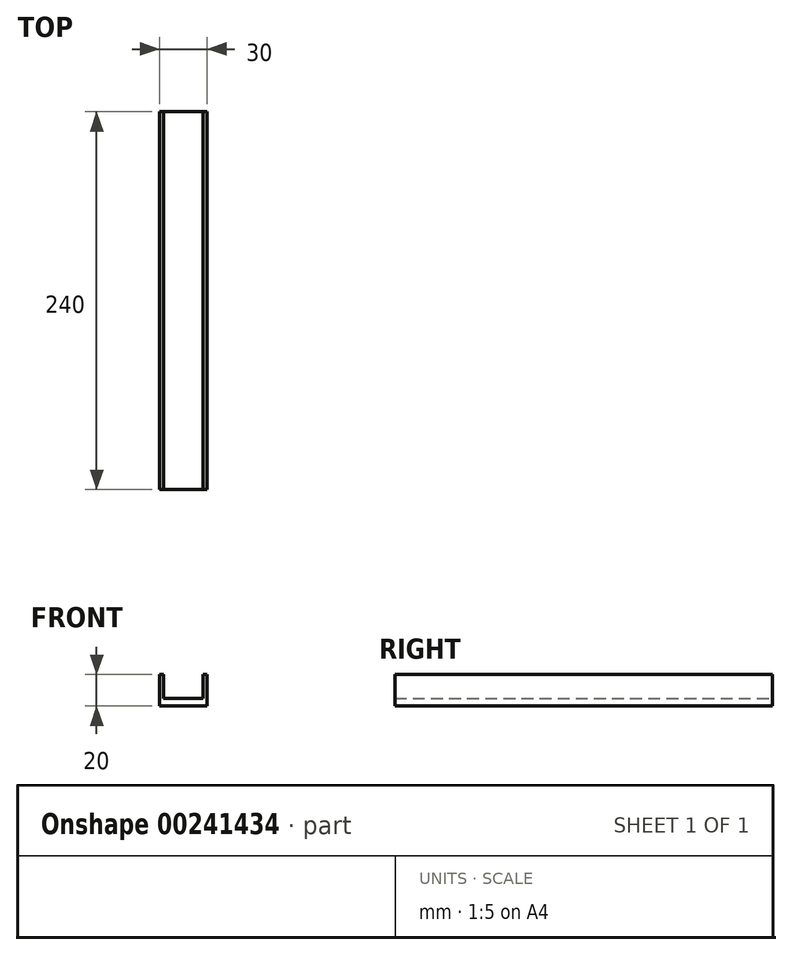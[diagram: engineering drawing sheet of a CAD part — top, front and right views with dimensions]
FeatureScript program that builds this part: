
annotation { "Feature Type Name" : "Feature", "Feature Type Description" : "" }
export const myFeature = defineFeature(function(context is Context, id is Id, definition is map)
    precondition{}
    {
        {
            var Q0;
            Q0=qCreatedBy(makeId("Front.planeOp"),FACE);
            var sketch = newSketch(context, id + "F0", { "sketchPlane" : qUnion([Q0])});
            skLineSegment(sketch, "E0.bottom", {"start": v(-15, 10) * mm, "end": v(15, 10) * mm});
            skLineSegment(sketch, "E0.top", {"start": v(-15, -10) * mm, "end": v(15, -10) * mm});
            skLineSegment(sketch, "E0.left", {"start": v(-15, 10) * mm, "end": v(-15, -10) * mm});
            skLineSegment(sketch, "E0.right", {"start": v(15, 10) * mm, "end": v(15, -10) * mm});
            skPoint(sketch, "E0.middle", {"position": v(0, 0) * mm});
            skLineSegment(sketch, "E1.bottom", {"start": v(-12.5, 10) * mm, "end": v(12.5, 10) * mm});
            skLineSegment(sketch, "E1.top", {"start": v(-12.5, -5) * mm, "end": v(12.5, -5) * mm});
            skLineSegment(sketch, "E1.left", {"start": v(-12.5, 10) * mm, "end": v(-12.5, -5) * mm});
            skLineSegment(sketch, "E1.right", {"start": v(12.5, 10) * mm, "end": v(12.5, -5) * mm});
            skSolve(sketch);
        }
        {
            var Q0;
            Q0=makeQuery(id+"F0.imprint","IMPRINT",FACE,{"disambiguationData":[TD([[makeQuery(id+"F0.imprint","IMPRINT",EDGE,{"derivedFrom":sQuery(id+"F0.wireOp",EDGE,"E0.top")}),1.0]])]});
            extrude(context, id + "F1", {"entities" : qUnion([Q0]), "depth" : 240 * mm});
        }
    });
